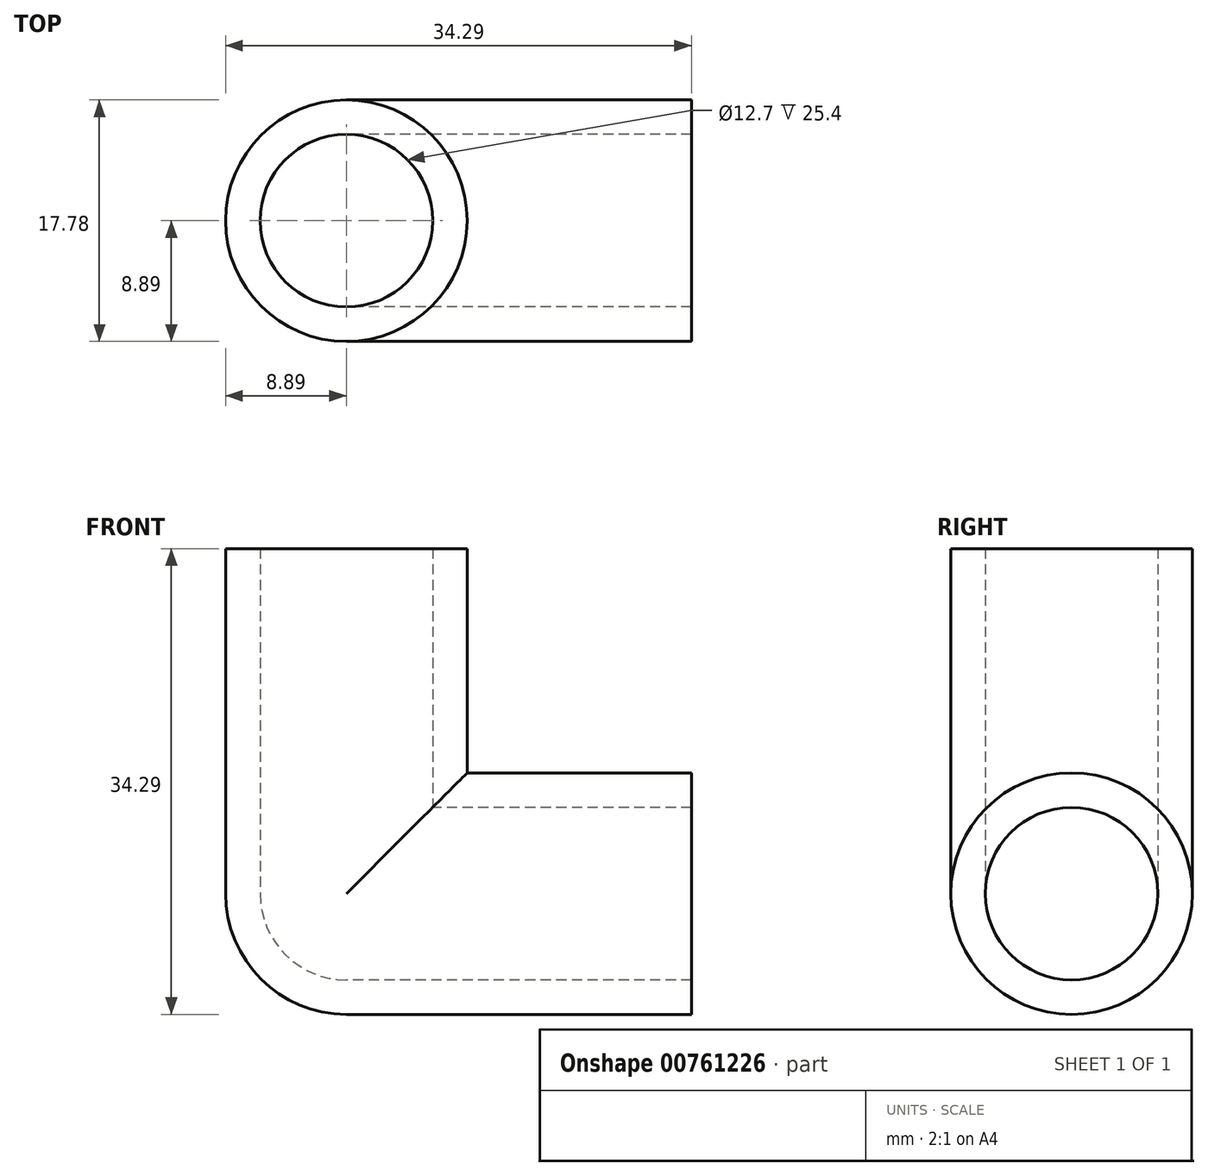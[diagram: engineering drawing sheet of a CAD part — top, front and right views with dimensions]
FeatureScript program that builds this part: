
annotation { "Feature Type Name" : "Feature", "Feature Type Description" : "" }
export const myFeature = defineFeature(function(context is Context, id is Id, definition is map)
    precondition{}
    {
        {
            var Q0;
            Q0=qCreatedBy(makeId("Top.planeOp"),FACE);
            var sketch = newSketch(context, id + "F0", { "sketchPlane" : qUnion([Q0])});
            skLineSegment(sketch, "E0", {"start": v(0, 0) * mm, "end": v(25.4, 0) * mm, "construction": true});
            skLineSegment(sketch, "E1", {"start": v(0, 0) * mm, "end": v(25.4, 0) * mm});
            skLineSegment(sketch, "E2", {"start": v(25.4, 0) * mm, "end": v(25.4, 8.89) * mm});
            skLineSegment(sketch, "E3", {"start": v(25.4, 8.9) * mm, "end": v(0, 8.89) * mm});
            skLineSegment(sketch, "E4", {"start": v(0, 8.89) * mm, "end": v(0, 0) * mm});
            skSolve(sketch);
        }
        {
            var Q0;
            Q0=makeQuery(id+"F0.imprint","IMPRINT",FACE,{"disambiguationData":[TD([[makeQuery(id+"F0.imprint","IMPRINT",EDGE,{"derivedFrom":sQuery(id+"F0.wireOp",EDGE,"E1")}),1.0]])]});
            var Q1;
            Q1=sQuery(id+"F0.wireOp",EDGE,"E1");
            revolve(context, id + "F1", {"surfaceOperationType" : NewSurfaceOperationType.NEW, "entities" : qUnion([Q0]), "axis" : qUnion([Q1]), "revolveType" : RevolveType.FULL});
        }
        {
            var Q0;
            Q0=qCreatedBy(makeId("Front.planeOp"),FACE);
            var sketch = newSketch(context, id + "F2", { "sketchPlane" : qUnion([Q0])});
            skLineSegment(sketch, "E5", {"start": v(0, 0) * mm, "end": v(0, 25.4) * mm});
            skLineSegment(sketch, "E6", {"start": v(-8.9, 25.4) * mm, "end": v(-8.89, 0) * mm});
            skLineSegment(sketch, "E7", {"start": v(-8.89, 0) * mm, "end": v(0, 0) * mm});
            skLineSegment(sketch, "E8", {"start": v(0, 25.4) * mm, "end": v(-8.9, 25.4) * mm});
            skSolve(sketch);
        }
        {
            var Q0;
            Q0=makeQuery(id+"F2.imprint","IMPRINT",FACE,{"disambiguationData":[TD([[makeQuery(id+"F2.imprint","IMPRINT",EDGE,{"derivedFrom":sQuery(id+"F2.wireOp",EDGE,"E6")}),1.0]])]});
            var Q1;
            Q1=sQuery(id+"F2.wireOp",EDGE,"E5");
            revolve(context, id + "F3", {"operationType" : NewBodyOperationType.ADD, "surfaceOperationType" : NewSurfaceOperationType.NEW, "entities" : qUnion([Q0]), "axis" : qUnion([Q1]), "revolveType" : RevolveType.FULL});
        }
        {
            var Q0;
            Q0=qCreatedBy(makeId("Front.planeOp"),FACE);
            var sketch = newSketch(context, id + "F4", { "sketchPlane" : qUnion([Q0])});
            skArc(sketch, "E9", {"start": v(-5.08, 0) * mm, "mid": v(-3.6, -3.6) * mm, "end": v(0, -5.08) * mm});
            skSolve(sketch);
        }
        {
            var Q0;
            Q0=makeQuery(id+"F3.opRevolve","SWEPT_FACE",FACE,{"disambiguationData":[OSD([sQuery(id+"F2.wireOp",EDGE,"E7")])]});
            var Q1;
            Q1=sQuery(id+"F4.wireOp",EDGE,"E9");
            sweep(context, id + "F5", {"operationType" : NewBodyOperationType.ADD, "profiles" : qUnion([Q0]), "path" : qUnion([Q1])});
        }
        {
            var Q0;
            Q0=makeQuery(id+"F3.opRevolve","SWEPT_FACE",FACE,{"disambiguationData":[OSD([sQuery(id+"F2.wireOp",EDGE,"E8")])]});
            var Q1;
            Q1=makeQuery(id+"F1.opRevolve","SWEPT_FACE",FACE,{"disambiguationData":[OSD([sQuery(id+"F0.wireOp",EDGE,"E2")])]});
            shell(context, id + "F6", {"entities" : qUnion([Q0, Q1]), "thickness" : 2.54 * mm});
        }
    });
